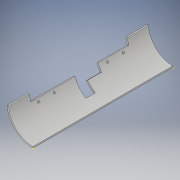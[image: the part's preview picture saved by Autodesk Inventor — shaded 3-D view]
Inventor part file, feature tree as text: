
AUTODESK INVENTOR PART (.ipt)
format: ipt  version: 2017 (Build 210142000, 142)  size: 193,024 bytes
history: native  units: in
note: dims shown in document units (in); Inventor stores cm internally (conversion verified against a paired STEP export)
features: sketch x10, extrude x5, plane x3, hole x1, mirror x1
ambient origin geometry x8: Origin, YZ Plane, XZ Plane, XY Plane, X Axis, Y Axis, Z Axis, Center Point
bodies: Solid1 (feature_tree)
feature tree (20):
  extrude  "Extrusion1"  Depth=2.0472in
  sketch  "Sketch4"  dims[d4=1.4173in d5=1.5354in]
  sketch  "Sketch5"  dims[d6=0.0in d7=0.0in]
  plane  "Work Plane3"
  sketch  "Sketch6"  dims[d9=11.811in d10=0.0in d27=0.0481in]
  sketch  "Sketch7"  dims[d28=2.1654in d30=5.9055in]
  hole  "Hole2"  [1 undecoded]
  extrude  "Extrusion2"  TaperAngle=0.0deg  [1 undecoded]
  plane  "Work Plane4"
  extrude  "Extrusion3"  Depth=0.0481in
  extrude  "Extrusion4"  Depth=2.1654in
  plane  "Work Plane5"
  mirror  "Mirror1"
  extrude  "Extrusion5"  Depth=1.3386in
  sketch  "Sketch1"  dims[d0=2.1654in d1=2.0472in]
  sketch  "Sketch8"  dims[d31=2.2441in d32=1.3386in]
  sketch  "Sketch9"  dims[d33=0.2644in]
  sketch  "Sketch10"  dims[d34=0.2644in]
  sketch  "Sketch11"  dims[d35=0.1732in d36=0.2362in d37=0.1575in d38=0.0787in d39=90.0deg d40=0.315in d41=0.8108in]
  sketch  "Sketch12"  dims[d42=5.9055in d43=1.2992in d46=0.5906in d47=1.9685in d48=0.3937in d49=0.0in d50=0.3937in d51=0.0in d52=2.0472in d53=2.1654in d54=15.0deg d55=1.7717in d56=0.0in d57=0.1718in d58=2.1654in d59=2.0472in d60=1.1811in d61=0.0in]
note: 2 required parameter values undecoded (feature->parameter linkage not recoverable at this tier; creation-order binding heuristic only, values carry confidence <= 0.55)
